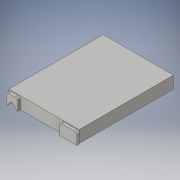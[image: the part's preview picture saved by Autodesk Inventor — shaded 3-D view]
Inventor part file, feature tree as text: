
AUTODESK INVENTOR PART (.ipt)
format: ipt  version: 2016 (Build 200138000, 138)  size: 162,816 bytes
history: native  units: mm
features: extrude x6, sketch x6, fillet x2
ambient origin geometry x8: Origin, YZ Plane, XZ Plane, XY Plane, X Axis, Y Axis, Z Axis, Center Point
bodies: Solid1 (feature_tree)
feature tree (14):
  extrude  "Extrusion1"  Depth=151.0mm
  extrude  "Extrusion2"  Depth=25.0mm
  extrude  "Extrusion3"  Depth=22.68928mm
  extrude  "Extrusion4"  Depth=10.0mm
  extrude  "Extrusion5"  Depth=25.0mm
  extrude  "Extrusion6"  Depth=2.0mm TaperAngle=0.0deg
  fillet  "Fillet1"  Radius=37.0mm
  fillet  "Fillet2"  Radius=6.0mm
  sketch  "Sketch1"  dims[d19=26.0mm d20=151.0mm]
  sketch  "Sketch2"  dims[d21=203.0mm d22=0.0mm d23=25.0mm]
  sketch  "Sketch3"  dims[d29=4.0mm d30=22.68928mm]
  sketch  "Sketch4"  dims[d31=8.726646mm d32=10.0mm]
  sketch  "Sketch5"  dims[d33=215.0mm d34=0.0mm d35=25.0mm]
  sketch  "Sketch6"  dims[d36=6.0mm d37=0.0mm d38=2.0mm d39=0.0mm d40=37.0mm d41=6.0mm d42=0.0mm d43=1.0mm d44=0.0mm d45=5.0mm d46=5.0mm]
